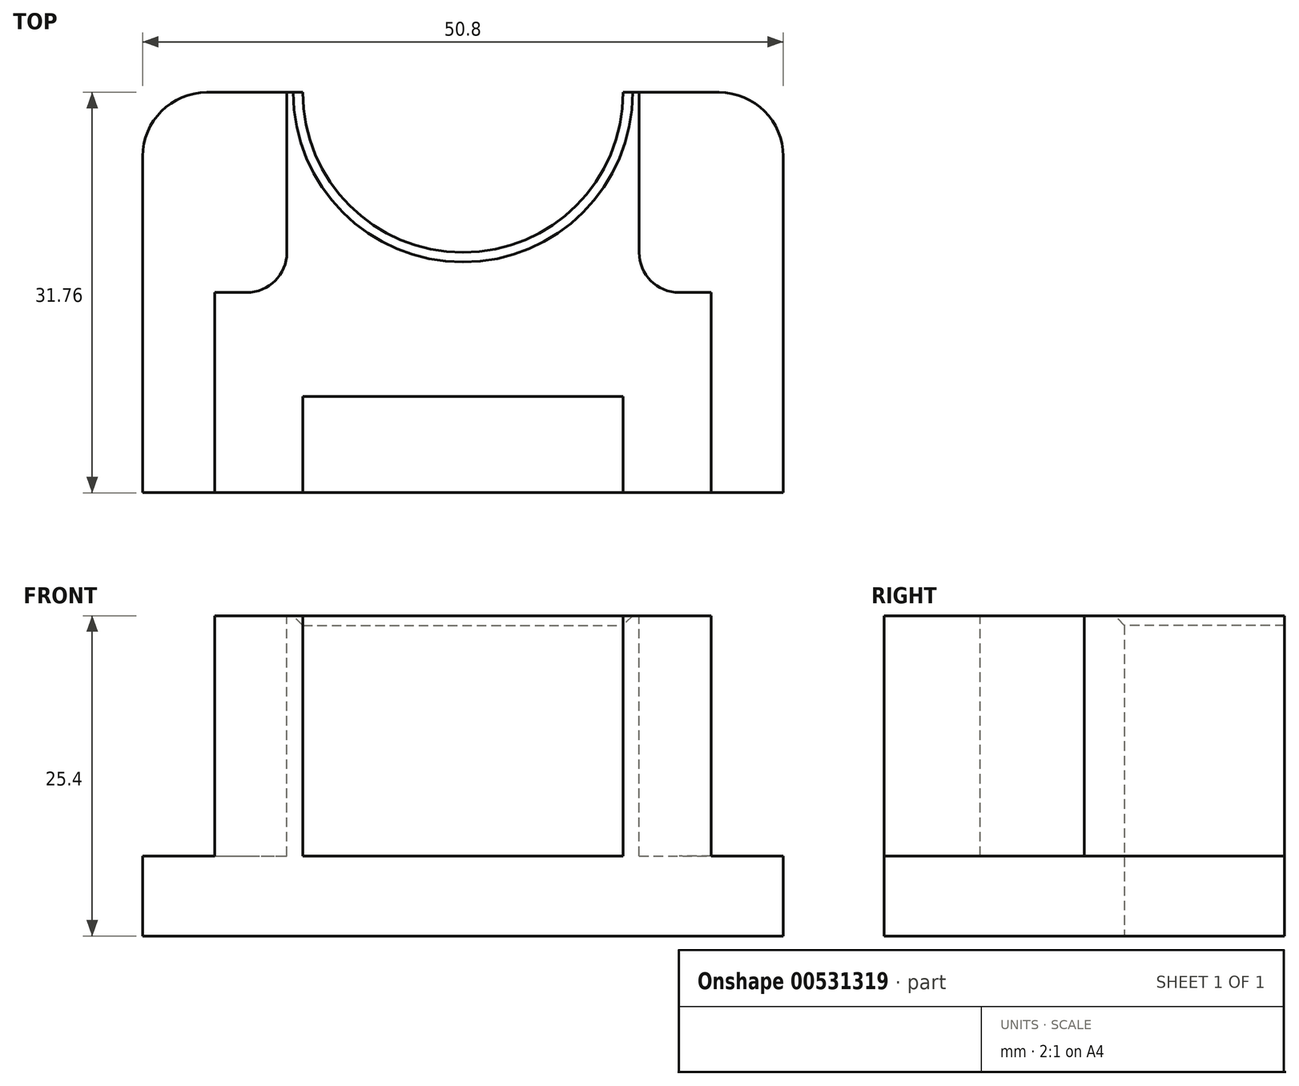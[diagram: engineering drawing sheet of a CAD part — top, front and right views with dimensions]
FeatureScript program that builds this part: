
annotation { "Feature Type Name" : "Feature", "Feature Type Description" : "" }
export const myFeature = defineFeature(function(context is Context, id is Id, definition is map)
    precondition{}
    {
        {
            var Q0;
            Q0=qCreatedBy(makeId("Top.planeOp"),FACE);
            var sketch = newSketch(context, id + "F0", { "sketchPlane" : qUnion([Q0])});
            skLineSegment(sketch, "E0.bottom", {"start": v(-25.4, 15.88) * mm, "end": v(25.4, 15.88) * mm});
            skLineSegment(sketch, "E0.top", {"start": v(-25.4, -15.88) * mm, "end": v(25.4, -15.88) * mm});
            skLineSegment(sketch, "E0.left", {"start": v(-25.4, 15.88) * mm, "end": v(-25.4, -15.88) * mm});
            skLineSegment(sketch, "E0.right", {"start": v(25.4, 15.88) * mm, "end": v(25.4, -15.88) * mm});
            skPoint(sketch, "E0.middle", {"position": v(0, 0) * mm});
            skCircle(sketch, "E1", {"center": v(0, 15.88) * mm, "radius": 12.7 * mm});
            skSolve(sketch);
        }
        {
            var Q0;
            Q0=makeQuery(id+"F0.imprint","IMPRINT",FACE,{"disambiguationData":[TD([[makeQuery(id+"F0.imprint","IMPRINT",EDGE,{"derivedFrom":sQuery(id+"F0.wireOp",EDGE,"E0.top")}),1.0]])]});
            extrude(context, id + "F1", {"entities" : qUnion([Q0]), "depth" : 25.4 * mm, "offsetDistance" : 25.4 * mm});
        }
        {
            var Q0;
            Q0=makeQuery(id+"F1.opExtrude","CAP_FACE",FACE,{"disambiguationData":[OSD([sQuery(id+"F0.wireOp",EDGE,"E0.bottom"),sQuery(id+"F0.wireOp",EDGE,"E0.top"),sQuery(id+"F0.wireOp",EDGE,"E0.left"),sQuery(id+"F0.wireOp",EDGE,"E0.right"),sQuery(id+"F0.wireOp",EDGE,"E1")])],"isStart":false});
            var sketch = newSketch(context, id + "F2", { "sketchPlane" : qUnion([Q0])});
            skLineSegment(sketch, "E2.bottom", {"start": v(-12.7, -8.25) * mm, "end": v(12.7, -8.25) * mm});
            skLineSegment(sketch, "E2.top", {"start": v(-12.7, -23.5) * mm, "end": v(12.7, -23.5) * mm});
            skLineSegment(sketch, "E2.left", {"start": v(-12.7, -8.25) * mm, "end": v(-12.7, -23.5) * mm});
            skLineSegment(sketch, "E2.right", {"start": v(12.7, -8.25) * mm, "end": v(12.7, -23.5) * mm});
            skPoint(sketch, "E2.middle", {"position": v(0, -15.88) * mm});
            skLineSegment(sketch, "E3", {"start": v(-25.4, -15.88) * mm, "end": v(-16.5, -15.88) * mm});
            skLineSegment(sketch, "E4", {"start": v(-16.5, -15.88) * mm, "end": v(-16.5, 0) * mm});
            skLineSegment(sketch, "E5", {"start": v(-16.5, 0) * mm, "end": v(-13.97, 0) * mm});
            skLineSegment(sketch, "E6", {"start": v(-13.97, 0) * mm, "end": v(-13.97, 15.88) * mm});
            skLineSegment(sketch, "E7", {"start": v(-13.97, 15.88) * mm, "end": v(-25.4, 15.88) * mm});
            skLineSegment(sketch, "E8", {"start": v(-25.4, 15.88) * mm, "end": v(-25.4, -15.88) * mm});
            skLineSegment(sketch, "E9.MirrorCS", {"start": v(13.97, 15.88) * mm, "end": v(25.4, 15.88) * mm});
            skLineSegment(sketch, "E10.MirrorCS", {"start": v(13.97, 0) * mm, "end": v(13.97, 15.88) * mm});
            skLineSegment(sketch, "E11.MirrorCS", {"start": v(16.5, 0) * mm, "end": v(13.97, 0) * mm});
            skLineSegment(sketch, "E12.MirrorCS", {"start": v(16.5, -15.88) * mm, "end": v(16.5, 0) * mm});
            skLineSegment(sketch, "E13.MirrorCS", {"start": v(25.4, -15.88) * mm, "end": v(16.5, -15.88) * mm});
            skLineSegment(sketch, "E14.MirrorCS", {"start": v(25.4, 15.88) * mm, "end": v(25.4, -15.88) * mm});
            skSolve(sketch);
        }
        {
            var Q0;
            {var subQ0=sQuery(id+"F2.wireOp",EDGE,"E2.bottom");Q0=makeQuery(id+"F2.imprint","IMPRINT",FACE,{"disambiguationData":[TD([[makeQuery(id+"F2.imprint","IMPRINT",EDGE,{"derivedFrom":subQ0}),-1.0]])]});}
            extrude(context, id + "F3", {"entities" : qUnion([Q0]), "operationType" : NewBodyOperationType.REMOVE, "oppositeDirection" : true, "depth" : 19.05 * mm, "offsetDistance" : 25.4 * mm});
        }
        {
            var Q0;
            Q0=makeQuery(id+"F1.opExtrude","CAP_FACE",FACE,{"disambiguationData":[OSD([sQuery(id+"F0.wireOp",EDGE,"E0.bottom"),sQuery(id+"F0.wireOp",EDGE,"E0.top"),sQuery(id+"F0.wireOp",EDGE,"E0.left"),sQuery(id+"F0.wireOp",EDGE,"E0.right"),sQuery(id+"F0.wireOp",EDGE,"E1")])],"isStart":false});
            var sketch = newSketch(context, id + "F4", { "sketchPlane" : qUnion([Q0])});
            skLineSegment(sketch, "E15", {"start": v(-25.4, -15.88) * mm, "end": v(-16.5, -15.88) * mm});
            skLineSegment(sketch, "E16", {"start": v(-16.5, -15.88) * mm, "end": v(-16.5, 0) * mm});
            skLineSegment(sketch, "E17", {"start": v(-16.5, 0) * mm, "end": v(-13.97, 0) * mm});
            skLineSegment(sketch, "E18", {"start": v(-13.97, 0) * mm, "end": v(-13.97, 15.88) * mm});
            skLineSegment(sketch, "E19", {"start": v(-13.97, 15.88) * mm, "end": v(-25.4, 15.88) * mm});
            skLineSegment(sketch, "E20", {"start": v(-25.4, 15.88) * mm, "end": v(-25.4, -15.88) * mm});
            skLineSegment(sketch, "E21.MirrorCS", {"start": v(13.97, 0) * mm, "end": v(13.97, 15.88) * mm});
            skLineSegment(sketch, "E22.MirrorCS", {"start": v(13.97, 15.88) * mm, "end": v(25.4, 15.88) * mm});
            skLineSegment(sketch, "E23.MirrorCS", {"start": v(25.4, 15.88) * mm, "end": v(25.4, -15.88) * mm});
            skLineSegment(sketch, "E24.MirrorCS", {"start": v(16.5, -15.88) * mm, "end": v(16.5, 0) * mm});
            skLineSegment(sketch, "E25.MirrorCS", {"start": v(25.4, -15.88) * mm, "end": v(16.5, -15.88) * mm});
            skLineSegment(sketch, "E26.MirrorCS", {"start": v(16.5, 0) * mm, "end": v(13.97, 0) * mm});
            skSolve(sketch);
        }
        {
            var Q0;
            Q0=makeQuery(id+"F4.imprint","IMPRINT",FACE,{"disambiguationData":[TD([[makeQuery(id+"F4.imprint","IMPRINT",EDGE,{"derivedFrom":sQuery(id+"F4.wireOp",EDGE,"E15")}),1.0]])]});
            var Q1;
            Q1=makeQuery(id+"F4.imprint","IMPRINT",FACE,{"disambiguationData":[TD([[makeQuery(id+"F4.imprint","IMPRINT",EDGE,{"derivedFrom":sQuery(id+"F4.wireOp",EDGE,"E21.MirrorCS")}),-1.0]])]});
            extrude(context, id + "F5", {"entities" : qUnion([Q0, Q1]), "operationType" : NewBodyOperationType.REMOVE, "oppositeDirection" : true, "depth" : 19.05 * mm, "offsetDistance" : 25.4 * mm});
        }
        {
            var Q0;
            Q0=makeQuery(id+"F1.opExtrude","SWEPT_EDGE",EDGE,{"disambiguationData":[OSD([sQuery(id+"F0.wireOp",EDGE,"E0.bottom"),sQuery(id+"F0.wireOp",EDGE,"E0.right")])]});
            var Q1;
            Q1=makeQuery(id+"F1.opExtrude","SWEPT_EDGE",EDGE,{"disambiguationData":[OSD([sQuery(id+"F0.wireOp",EDGE,"E0.bottom"),sQuery(id+"F0.wireOp",EDGE,"E0.left")])]});
            fillet(context, id + "F6", {"entities" : qUnion([Q0, Q1]), "radius" : 5.08 * mm, "tangentPropagation" : true, "allowEdgeOverflow" : false});
        }
        {
            var Q0;
            Q0=makeQuery(id+"F5.boolean.opBoolean","COPY",FACE,{"derivedFrom":makeQuery(id+"F5.opExtrude","SWEPT_FACE",FACE,{"disambiguationData":[OSD([sQuery(id+"F4.wireOp",EDGE,"E24.MirrorCS")])]})});
            extrude(context, id + "F7", {"entities" : qUnion([Q0]), "operationType" : NewBodyOperationType.ADD, "depth" : 3.17 * mm, "offsetDistance" : 25.4 * mm});
        }
        {
            var Q0;
            Q0=makeQuery(id+"F5.boolean.opBoolean","COPY",FACE,{"derivedFrom":makeQuery(id+"F5.opExtrude","SWEPT_FACE",FACE,{"disambiguationData":[OSD([sQuery(id+"F4.wireOp",EDGE,"E16")])]})});
            extrude(context, id + "F8", {"entities" : qUnion([Q0]), "operationType" : NewBodyOperationType.ADD, "depth" : 3.17 * mm, "offsetDistance" : 25.4 * mm});
        }
        {
            var Q0;
            Q0=makeQuery(id+"F5.boolean.opBoolean","COPY",EDGE,{"derivedFrom":makeQuery(id+"F5.opExtrude","SWEPT_EDGE",EDGE,{"disambiguationData":[OSD([sQuery(id+"F4.wireOp",EDGE,"E17"),sQuery(id+"F4.wireOp",EDGE,"E18")])]})});
            var Q1;
            Q1=makeQuery(id+"F5.boolean.opBoolean","COPY",EDGE,{"derivedFrom":makeQuery(id+"F5.opExtrude","SWEPT_EDGE",EDGE,{"disambiguationData":[OSD([sQuery(id+"F4.wireOp",EDGE,"E21.MirrorCS"),sQuery(id+"F4.wireOp",EDGE,"E26.MirrorCS")])]})});
            fillet(context, id + "F9", {"entities" : qUnion([Q0, Q1]), "radius" : 3.17 * mm, "tangentPropagation" : true, "allowEdgeOverflow" : false});
        }
        {
            var Q0;
            Q0=makeQuery(id+"F3.boolean.opBoolean","COPY",EDGE,{"derivedFrom":makeQuery(id+"F3.opExtrude","CAP_EDGE",EDGE,{"disambiguationData":[OSD([sQuery(id+"F2.wireOp",EDGE,"E2.bottom")])],"isStart":true})});
            var Q1;
            Q1=makeQuery(id+"F3.boolean.opBoolean","COPY",EDGE,{"derivedFrom":makeQuery(id+"F3.opExtrude","CAP_EDGE",EDGE,{"disambiguationData":[OSD([sQuery(id+"F2.wireOp",EDGE,"E2.right")])],"isStart":true})});
            var Q2;
            Q2=makeQuery(id+"F3.boolean.opBoolean","COPY",EDGE,{"derivedFrom":makeQuery(id+"F3.opExtrude","CAP_EDGE",EDGE,{"disambiguationData":[OSD([sQuery(id+"F2.wireOp",EDGE,"E2.left")])],"isStart":true})});
            var Q3;
            Q3=makeQuery(id+"F1.opExtrude","CAP_EDGE",EDGE,{"disambiguationData":[OSD([sQuery(id+"F0.wireOp",EDGE,"E1")])],"isStart":false});
            chamfer(context, id + "F10", {"entities" : qUnion([Q0, Q1, Q2, Q3]), "width" : 0.76 * mm, "tangentPropagation" : true});
        }
    });
